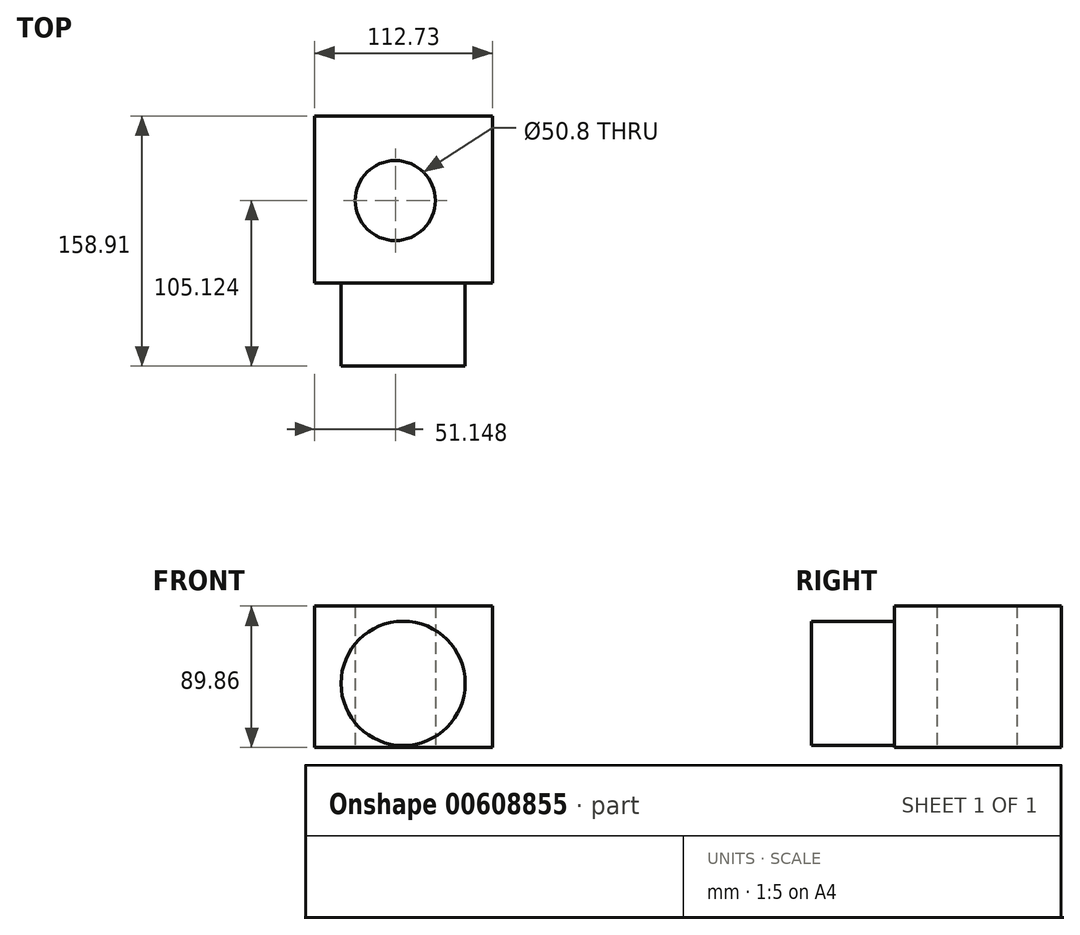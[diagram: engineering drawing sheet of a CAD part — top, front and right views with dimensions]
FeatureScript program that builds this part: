
annotation { "Feature Type Name" : "Feature", "Feature Type Description" : "" }
export const myFeature = defineFeature(function(context is Context, id is Id, definition is map)
    precondition{}
    {
        {
            var Q0;
            Q0=qCreatedBy(makeId("Top.planeOp"),FACE);
            var sketch = newSketch(context, id + "F0", { "sketchPlane" : qUnion([Q0])});
            skLineSegment(sketch, "E0.bottom", {"start": v(0, 0) * mm, "end": v(-112.73, 0) * mm});
            skLineSegment(sketch, "E0.top", {"start": v(0, -106.2) * mm, "end": v(-112.73, -106.2) * mm});
            skLineSegment(sketch, "E0.left", {"start": v(0, 0) * mm, "end": v(0, -106.2) * mm});
            skLineSegment(sketch, "E0.right", {"start": v(-112.73, 0) * mm, "end": v(-112.73, -106.2) * mm});
            skLineSegment(sketch, "E1.bottom", {"start": v(-56.36, -106.2) * mm, "end": v(-43.28, -106.2) * mm});
            skLineSegment(sketch, "E1.top", {"start": v(-56.36, -116.11) * mm, "end": v(-43.28, -116.11) * mm});
            skLineSegment(sketch, "E1.left", {"start": v(-56.36, -106.2) * mm, "end": v(-56.36, -116.11) * mm});
            skLineSegment(sketch, "E1.right", {"start": v(-43.28, -106.2) * mm, "end": v(-43.28, -116.11) * mm});
            skSolve(sketch);
        }
        {
            var Q0;
            Q0=makeQuery(id+"F0.imprint","IMPRINT",FACE,{"disambiguationData":[TD([[makeQuery(id+"F0.imprint","IMPRINT",EDGE,{"derivedFrom":sQuery(id+"F0.wireOp",EDGE,"E0.bottom")}),1.0]])]});
            var sketch = newSketch(context, id + "F1", { "sketchPlane" : qUnion([Q0])});
            skLineSegment(sketch, "E2.0", {"start": v(-112.73, 0) * mm, "end": v(-112.73, -106.2) * mm});
            skLineSegment(sketch, "E3.0", {"start": v(0, -106.2) * mm, "end": v(-112.73, -106.2) * mm});
            skSolve(sketch);
        }
        {
            var Q0;
            Q0 = qSketchRegion(id + "F1", true);
            var Q1;
            Q1=makeQuery(id+"F0.imprint","IMPRINT",FACE,{"disambiguationData":[TD([[makeQuery(id+"F0.imprint","IMPRINT",EDGE,{"derivedFrom":sQuery(id+"F0.wireOp",EDGE,"E0.bottom")}),1.0]])]});
            extrude(context, id + "F2", {"entities" : qUnion([Q0, Q1]), "depth" : 89.86 * mm, "offsetDistance" : 25.4 * mm});
        }
        {
            var Q0;
            Q0=makeQuery(id+"F2.opExtrude","SWEPT_FACE",FACE,{"disambiguationData":[OSD([sQuery(id+"F0.wireOp",EDGE,"E0.bottom")])]});
            var sketch = newSketch(context, id + "F3", { "sketchPlane" : qUnion([Q0])});
            skCircle(sketch, "E4", {"center": v(56.62, 40.8) * mm, "radius": 39.44 * mm});
            skSolve(sketch);
        }
        {
            var Q0;
            Q0=makeQuery(id+"F3.imprint","IMPRINT",FACE,{"disambiguationData":[TD([[makeQuery(id+"F3.imprint","IMPRINT",EDGE,{"derivedFrom":sQuery(id+"F3.wireOp",EDGE,"E4")}),1.0]])]});
            extrude(context, id + "F4", {"entities" : qUnion([Q0]), "operationType" : NewBodyOperationType.ADD, "oppositeDirection" : true, "depth" : 158.9 * mm, "offsetDistance" : 25.4 * mm});
        }
        {
            var Q0;
            Q0=qCreatedBy(makeId("Top.planeOp"),FACE);
            var sketch = newSketch(context, id + "F5", { "sketchPlane" : qUnion([Q0])});
            skCircle(sketch, "E5", {"center": v(-61.58, -53.79) * mm, "radius": 35.92 * mm});
            skSolve(sketch);
        }
        {
            var Q0;
            Q0=sQuery(id+"F5.wireOp",VERTEX,"E5.center");
            var Q1;
            Q1=makeQuery(id+"F2.opExtrude","SWEPT_BODY",BODY,{"disambiguationData":[OSD([sQuery(id+"F0.wireOp",EDGE,"E0.bottom"),sQuery(id+"F0.wireOp",EDGE,"E0.top"),sQuery(id+"F0.wireOp",EDGE,"E0.left"),sQuery(id+"F0.wireOp",EDGE,"E0.right"),sQuery(id+"F0.wireOp",EDGE,"E1.bottom")])]});
            hole(context, id + "F6", {"style" : HoleStyle.SIMPLE, "endStyle" : HoleEndStyle.THROUGH, "oppositeDirection" : true, "holeDiameter" : 50.8 * mm, "majorDiameter" : 6.35 * mm, "isTappedThrough" : true, "tappedDepth" : 12.7 * mm, "tapClearance" : 3, "locations" : qUnion([Q0]), "scope" : qUnion([Q1])});
        }
    });
